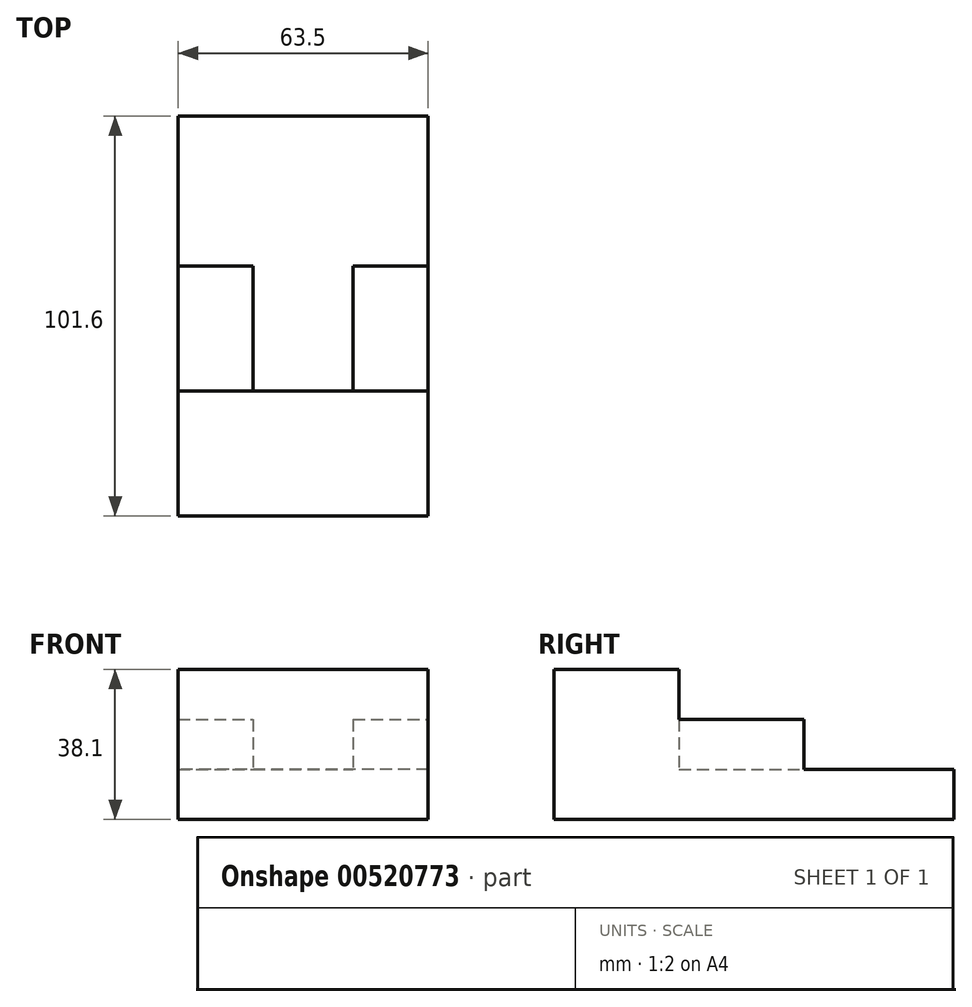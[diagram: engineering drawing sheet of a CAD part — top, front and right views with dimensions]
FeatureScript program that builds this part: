
annotation { "Feature Type Name" : "Feature", "Feature Type Description" : "" }
export const myFeature = defineFeature(function(context is Context, id is Id, definition is map)
    precondition{}
    {
        {
            var Q0;
            Q0=qCreatedBy(makeId("Top.planeOp"),FACE);
            var sketch = newSketch(context, id + "F0", { "sketchPlane" : qUnion([Q0])});
            skLineSegment(sketch, "E0.bottom", {"start": v(31.75, 50.8) * mm, "end": v(-31.75, 50.8) * mm});
            skLineSegment(sketch, "E0.top", {"start": v(31.75, -50.8) * mm, "end": v(-31.75, -50.8) * mm});
            skLineSegment(sketch, "E0.left", {"start": v(31.75, 50.8) * mm, "end": v(31.75, -50.8) * mm});
            skLineSegment(sketch, "E0.right", {"start": v(-31.75, 50.8) * mm, "end": v(-31.75, -50.8) * mm});
            skPoint(sketch, "E0.middle", {"position": v(0, 0) * mm});
            skSolve(sketch);
        }
        {
            var Q0;
            Q0=makeQuery(id+"F0.imprint","IMPRINT",FACE,{"disambiguationData":[TD([[makeQuery(id+"F0.imprint","IMPRINT",EDGE,{"derivedFrom":sQuery(id+"F0.wireOp",EDGE,"E0.bottom")}),1.0]])]});
            extrude(context, id + "F1", {"entities" : qUnion([Q0]), "depth" : 12.7 * mm, "offsetDistance" : 25.4 * mm});
        }
        {
            var Q0;
            Q0=makeQuery(id+"F1.opExtrude","CAP_FACE",FACE,{"disambiguationData":[OSD([sQuery(id+"F0.wireOp",EDGE,"E0.bottom"),sQuery(id+"F0.wireOp",EDGE,"E0.top"),sQuery(id+"F0.wireOp",EDGE,"E0.left"),sQuery(id+"F0.wireOp",EDGE,"E0.right")])],"isStart":false});
            var sketch = newSketch(context, id + "F2", { "sketchPlane" : qUnion([Q0])});
            skLineSegment(sketch, "E1.bottom", {"start": v(31.75, 12.7) * mm, "end": v(12.7, 12.7) * mm});
            skLineSegment(sketch, "E1.top", {"start": v(31.75, -50.8) * mm, "end": v(12.7, -50.8) * mm});
            skLineSegment(sketch, "E1.left", {"start": v(31.75, 12.7) * mm, "end": v(31.75, -50.8) * mm});
            skLineSegment(sketch, "E1.right", {"start": v(12.7, 12.7) * mm, "end": v(12.7, -50.8) * mm});
            skLineSegment(sketch, "E2.bottom", {"start": v(-31.75, -50.8) * mm, "end": v(-12.7, -50.8) * mm});
            skLineSegment(sketch, "E2.top", {"start": v(-31.75, 12.7) * mm, "end": v(-12.7, 12.7) * mm});
            skLineSegment(sketch, "E2.left", {"start": v(-31.75, -50.8) * mm, "end": v(-31.75, 12.7) * mm});
            skLineSegment(sketch, "E2.right", {"start": v(-12.7, -50.8) * mm, "end": v(-12.7, 12.7) * mm});
            skLineSegment(sketch, "E3.bottom", {"start": v(-12.7, -19.05) * mm, "end": v(12.7, -19.05) * mm});
            skLineSegment(sketch, "E3.top", {"start": v(-12.7, -50.8) * mm, "end": v(12.7, -50.8) * mm});
            skLineSegment(sketch, "E3.left", {"start": v(-12.7, -19.05) * mm, "end": v(-12.7, -50.8) * mm});
            skLineSegment(sketch, "E3.right", {"start": v(12.7, -19.05) * mm, "end": v(12.7, -50.8) * mm});
            skSolve(sketch);
        }
        {
            var Q0;
            Q0=makeQuery(id+"F2.imprint","IMPRINT",FACE,{"disambiguationData":[TD([[makeQuery(id+"F2.imprint","IMPRINT",EDGE,{"derivedFrom":sQuery(id+"F2.wireOp",EDGE,"E1.bottom")}),1.0]])]});
            var Q1;
            Q1=makeQuery(id+"F2.imprint","IMPRINT",FACE,{"disambiguationData":[TD([[makeQuery(id+"F2.imprint","IMPRINT",EDGE,{"derivedFrom":sQuery(id+"F2.wireOp",EDGE,"E2.bottom")}),-1.0]])]});
            var Q2;
            Q2=makeQuery(id+"F2.imprint","IMPRINT",FACE,{"disambiguationData":[TD([[makeQuery(id+"F2.imprint","IMPRINT",EDGE,{"derivedFrom":sQuery(id+"F2.wireOp",EDGE,"E3.bottom")}),-1.0]])]});
            extrude(context, id + "F3", {"entities" : qUnion([Q0, Q1, Q2]), "operationType" : NewBodyOperationType.ADD, "depth" : 12.7 * mm, "offsetDistance" : 25.4 * mm});
        }
        {
            var Q0;
            Q0=makeQuery(id+"F3.opExtrude","CAP_FACE",FACE,{"disambiguationData":[OSD([sQuery(id+"F2.wireOp",EDGE,"E1.bottom"),sQuery(id+"F2.wireOp",EDGE,"E1.top"),sQuery(id+"F2.wireOp",EDGE,"E1.left"),sQuery(id+"F2.wireOp",EDGE,"E1.right"),sQuery(id+"F2.wireOp",EDGE,"E2.bottom"),sQuery(id+"F2.wireOp",EDGE,"E2.top"),sQuery(id+"F2.wireOp",EDGE,"E2.left"),sQuery(id+"F2.wireOp",EDGE,"E2.right"),sQuery(id+"F2.wireOp",EDGE,"E3.bottom"),sQuery(id+"F2.wireOp",EDGE,"E3.top")])],"isStart":false});
            var sketch = newSketch(context, id + "F4", { "sketchPlane" : qUnion([Q0])});
            skLineSegment(sketch, "E4.bottom", {"start": v(31.75, -50.8) * mm, "end": v(-31.75, -50.8) * mm});
            skLineSegment(sketch, "E4.top", {"start": v(31.75, -19.05) * mm, "end": v(-31.75, -19.05) * mm});
            skLineSegment(sketch, "E4.left", {"start": v(31.75, -50.8) * mm, "end": v(31.75, -19.05) * mm});
            skLineSegment(sketch, "E4.right", {"start": v(-31.75, -50.8) * mm, "end": v(-31.75, -19.05) * mm});
            skSolve(sketch);
        }
        {
            var Q0;
            Q0=makeQuery(id+"F4.imprint","IMPRINT",FACE,{"disambiguationData":[TD([[makeQuery(id+"F4.imprint","IMPRINT",EDGE,{"derivedFrom":sQuery(id+"F4.wireOp",EDGE,"E4.bottom")}),-1.0]])]});
            extrude(context, id + "F5", {"entities" : qUnion([Q0]), "operationType" : NewBodyOperationType.ADD, "depth" : 12.7 * mm, "offsetDistance" : 25.4 * mm});
        }
    });
